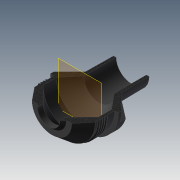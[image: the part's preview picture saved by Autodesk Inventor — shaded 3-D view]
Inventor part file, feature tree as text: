
AUTODESK INVENTOR PART (.ipt)
format: ipt  version: 2020 (Build 240168000, 168)  size: 457,728 bytes
history: native  units: mm
features: sketch x17, extrude x10, revolve x5, projected_geometry x5, chamfer x4, plane x4, helix x2, split x1, pattern_circular x1
ambient origin geometry x8: Origin, YZ Plane, XZ Plane, XY Plane, X Axis, Y Axis, Z Axis, Center Point
bodies: Solid1 (feature_tree)
feature tree (49):
  extrude  "Extrusion1"  Depth=2.0mm
  chamfer  "Chamfer1"  Distance=2.0mm
  revolve  "Revolution1"  [1 undecoded]
  extrude  "Extrusion2"  Depth=18.75mm
  sketch  "Sketch6"  dims[d17=1.6mm]
  helix  "Coil2"  [1 undecoded]
  chamfer  "Chamfer4"  Distance=10.0mm
  chamfer  "Chamfer5"  Distance=0.65mm Angle=45.0deg
  extrude  "Extrusion4"  Depth=42.0mm
  extrude  "Extrusion6"  Depth=3.3mm
  extrude  "Extrusion7"  Depth=1.2mm
  helix  "Coil3"  [1 undecoded]
  extrude  "Extrusion8"  Depth=3.0mm TaperAngle=0.0deg
  revolve  "Revolution2"  [1 undecoded]
  plane  "Work Plane2"
  split  "Split1"
  revolve  "Revolution3"  [1 undecoded]
  plane  "Work Plane3"
  plane  "Work Plane4"
  extrude  "Extrusion10"  Depth=10.0mm
  extrude  "Extrusion11"  Depth=10.0mm
  revolve  "Revolution4"  [1 undecoded]
  extrude  "Extrusion12"  TaperAngle=135.0deg  [1 undecoded]
  revolve  "Revolution5"  Angle=90.0deg
  plane  "Work Plane5"
  extrude  "Extrusion13"  TaperAngle=0.0deg  [1 undecoded]
  chamfer  "Chamfer7"  Distance=11.25mm
  pattern_circular  "Circular Pattern2"  Count=2  [1 undecoded]
  sketch  "Sketch1"  dims[d0=18.0mm d1=2.0mm d2=2.0mm d3=0.0mm]
  sketch  "Sketch4"  dims[d4=2.0mm d5=2.0mm d6=45.0deg d10=12.25mm]
  sketch  "Sketch5"  dims[d11=8.0mm d12=18.75mm d14=1.5mm]
  projected_geometry  "Projected Loop1"
  sketch  "Sketch8"  dims[d18=90.0deg d19=10.0mm d20=0.0mm]
  sketch  "Sketch9"  dims[d21=1.0mm]
  sketch  "Sketch10"  dims[d22=1.0mm]
  sketch  "Sketch11"  dims[d23=1.5mm]
  sketch  "Sketch12"  dims[d24=0.8mm]
  sketch  "Sketch13"  dims[d42=0.1mm]
  sketch  "Sketch14"  dims[d43=1.5mm]
  sketch  "Sketch16"  dims[d44=6.0mm d45=10.0mm d46=0.0mm d47=90.0deg d48=90.0deg d49=0.0mm d50=0.0mm d51=0.65mm d52=4.0mm d53=45.0deg]
  sketch  "Sketch17"  dims[d54=0.65mm d55=4.0mm d56=45.0deg d57=42.0mm]
  projected_geometry  "Projected Loop3"
  sketch  "Sketch18"  dims[d58=28.0mm d59=0.0mm d60=3.3mm]
  sketch  "Sketch19"  dims[d61=1.2mm d62=1.2mm d65=12.0mm d66=0.0mm]
  sketch  "Sketch20"  dims[d67=25.0mm d68=3.0mm d69=0.0mm]
  projected_geometry  "Projected Loop4"
  projected_geometry  "Projected Loop5"
  sketch  "Sketch21"  dims[d73=1.5mm d74=1.0mm d75=0.8mm d76=1.5mm d77=28.0mm d78=10.0mm d79=0.0mm d80=90.0deg d81=90.0deg d82=0.0mm d83=0.0mm d84=45.0mm d85=20.0mm d86=0.0mm d87=135.0deg d88=90.0deg d89=0.0mm d91=11.25mm d92=20.0mm d93=11.0mm d94=1.6mm d95=90.0deg d96=-20.0mm d108=-17.3mm d109=42.0mm d110=4.8mm d111=0.0mm d112=31.068147mm d113=21.0mm d115=2.8mm d116=0.0mm d117=0.473mm d118=90.0deg d119=2.8mm d120=0.0mm d121=135.0deg d122=90.0deg d123=-32.0mm d124=4.363323mm d125=10.0mm d126=0.0mm d127=6.5mm d128=9.75mm d129=45.0deg d130=60.0mm d131=360.0deg d70=0.5mm d71=0.872665mm d72=0.5mm d90=0.872665mm]
  projected_geometry  "Projected Loop6"
note: 9 required parameter values undecoded (feature->parameter linkage not recoverable at this tier; creation-order binding heuristic only, values carry confidence <= 0.55)